# Revit family: Faucet_Touchless-Lavatory-KOHLER-KUMIN-K-18656T_1
name_source: partatom
category: Plumbing Fixtures
revit_build: Autodesk Revit 2017 (Build: 20160225_1515(x64)
units: mm (PartAtom-declared; Revit-internal decimal feet)

## family parameters
Cut with Voids When Loaded = No
Host = Face
OmniClass Number = 23.31.11.00
OmniClass Title = Faucets
Part Type = Normal
Room Calculation Point = No
Round Connector Dimension = Use Diameter
Shared = No

## types (4) — shared parameters
ADA Compliant = No
Assembly Code = D2010
CW Connection = Yes
Cold Water Inlet = Cold Water Inlet
Date Modified = 5/10/2021
Default Elevation = 36"
Drain Included = Yes
Finish = Kohler-Metal-CP-Polished_Chrome
HW Connection = No
Height = 5 1/16"
Hot Water Inlet = Hot Water Inlet
Length = 5 5/16"
Manufacturer = KOHLER Co.
Master Format 2014 = 22 41 39
Master Format 2014 Name = Residential Faucets, Supplies, and Trim
Material = Premium Metal construction
Product Name = KUMIN
Spout Reach = 5 5/16"
URL = http://www.kohler.com.cn
Vent Connection = No
Waste Connection = No
Waste Water Outlet = Waste Water Outlet
WaterSense Certified = No
Width = 1 15/16"

## per-type parameters (varying)
| type | Description | Flow Rate | Model | Pressure | Type |
| 0.5 GPM, 60 psi, CP- Polished Chrome | SENSOR FAUCET- COLD, DC, W/ P, 0.5 GPM | 1 GPM | K-18656T-CP | 60.00 psi | 1 |
| 0.35 GPM, 60 psi, CP- Polished Chrome | SENSOR FAUCET- COLD, DC, W/ P, 0.35 GPM | 0 GPM | K-18656T-S3-CP | 60.00 psi | 2 |
| 0.35 GPM, 45 psi, CP-Polished_Chrome | SENSOR FAUCET- COLD, DC, W/ P, 0.35 GPM | 0 GPM | K-18656T-BS3-CP | 45.00 psi | 3 |
| 0.26 GPM, 45 psi, CP- Polished Chrome | SENSOR FAUCET- COLD, DC, W/ P, 0.26 GPM | 0 GPM | K-18656T-BS5-CP | 45.00 psi | 4 |

## geometry (parser evidence)
native form markers: Sweep x6
no freeform markers — native parametric forms only
